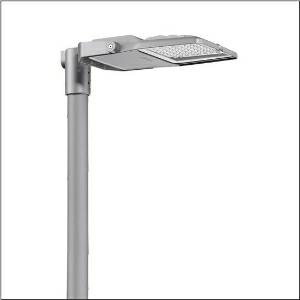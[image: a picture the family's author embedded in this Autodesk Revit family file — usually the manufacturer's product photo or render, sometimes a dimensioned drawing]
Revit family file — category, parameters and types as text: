
# Revit family: floodlight_fl_21_mini___pl52_5xa7776d4d3a_084d
name_source: partatom
category: Lighting Fixtures
units: mm (PartAtom-declared; Revit-internal decimal feet)

## family parameters
Cut with Voids When Loaded = No
Host = Face
Light Source = No
Part Type = Normal
Room Calculation Point = No
Round Connector Dimension = Use Diameter
Shared = No

## types (1)
- --- (1 x LED, 18600 lm, 142.9 W, 4000K)
    Apparent Load = 143 VA
    CIE Flux Codes = 26 60 98 100 100
    Color Rendering = 70
    Color Temperature = 4000K
    Default Elevation = 1800 mm
    Description = Floodlight FL 21 mini, floodlight, primary light control with lens, of PMMA, primary optical cover: protective disc, of toughened safety glass, transparent, light distribution: PL52, light emission: direct distribution, installation type: surface-mounted, LED, High Power LED, rated luminous flux: 18.600lm, luminous efficacy: 130lm/W, light colour: 740, colour temperature: 4000K, control gear: D4iSmart Interface (Zhaga), control: overheat protection, constant luminous flux control, time-dependent luminous flux control, flexible luminous flux parameterisation, pre-setting: logarithmic dimming characteristic, with terminal, 6-pole, mains connection: 220..240V, AC, 50/60Hz, start of lifetime: 143W, end of service life: 151W, reduction: 63W, mast bracket, of diecast aluminium, powder-coated, Siteco® metallic grey (DB 702S), corrosivity category C5 mid according to DIN EN ISO 12944, suitable for swimming pools, chlorine-resistant, sealing non-destructively replaceable, mast bracket, of steel, galvanised, powder-coated, Siteco® metallic grey (DB 702S), Smart Interface below and above, protection rating (complete): IP66, insulation class (complete): insulation class II (safety insulation), certification: CE, ENEC, VDE, protection symbol: D, impact resistance: IK08, permissible operating ambient temperature: -40..+40°C, permissible operating ambient temperature for outdoor applications: -40..+50°C, standard: DIN EN 12944, LABS conformity tested according to VDMA 24364:2018-05, packaging unit: 1 piece

Light Distribution: PL52
    Height = 70 mm
    Lamp = 1 x LED
    Lamp Light Flux = 18600 lm
    Lamp Power = 142.9 W
    Lamp count = 1
    Length = 485 mm
    Luminous efficacy = 130 lm/W
    Manufacturer = Siteco
    ModVariant = No
    Model = 5XA7776D4D3A
    Number of Poles = 1
    OnlyDefault = Yes
    Power Factor = 1
    Product Name = Floodlight FL 21 mini | PL52
    Product group = floodlight | pylon annexe
    ProductGroupID = 6201
    Protection Class = Protection class II
    Protection Degree = IP 66
    RLX_Detail_Level = 1
    RLX_Emergency_Light_Flux = 0 lm
    RLX_Emergency_Type = 0
    RLX_Emergency_Type_DB = No
    RlxData = <blob elided: 101485 chars, md5=082ca724>
    Socket = socket
    Standby Power = 0 W
    System Light Flux = 18600 lm
    System Power = 143 W
    Type Comments = factory setting: luminous flux: 100 % | dim-lin: 254 | 730 mA
    Type Image = l_1007125.jpg
    URL = http://relux.com
    VarID = @adj_116931
    Voltage = 0 V
    Weight = 0.00 kg
    Width = 337 mm

## geometry (parser evidence)
native form markers: Blend x4, Sweep x14
no freeform markers — native parametric forms only
